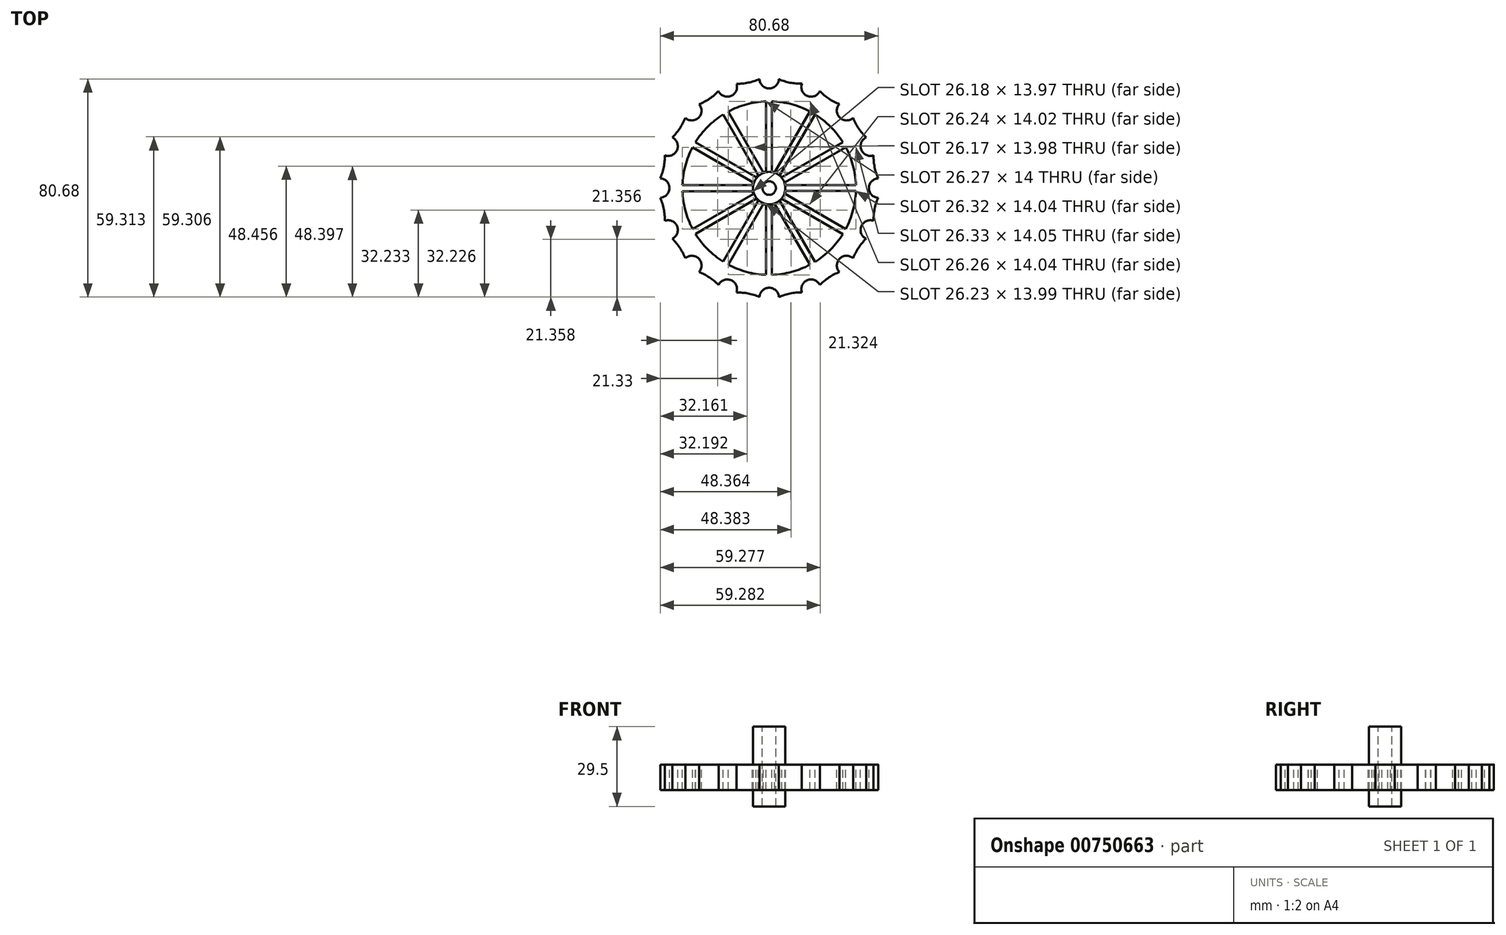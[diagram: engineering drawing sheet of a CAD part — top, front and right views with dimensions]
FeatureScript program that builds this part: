
annotation { "Feature Type Name" : "Feature", "Feature Type Description" : "" }
export const myFeature = defineFeature(function(context is Context, id is Id, definition is map)
    precondition{}
    {
        {
            var Q0;
            Q0=qCreatedBy(makeId("Front.planeOp"),FACE);
            var sketch = newSketch(context, id + "F0", { "sketchPlane" : qUnion([Q0])});
            skLineSegment(sketch, "E0", {"start": v(2.5, 29.5) * mm, "end": v(2.5, 0) * mm});
            skLineSegment(sketch, "E1", {"start": v(2.5, 0) * mm, "end": v(6, 0) * mm});
            skLineSegment(sketch, "E2", {"start": v(6, 0) * mm, "end": v(6, 6) * mm});
            skLineSegment(sketch, "E3", {"start": v(6, 6) * mm, "end": v(40.5, 6) * mm});
            skLineSegment(sketch, "E4", {"start": v(40.5, 6) * mm, "end": v(40.5, 15.5) * mm});
            skLineSegment(sketch, "E5", {"start": v(40.5, 15.5) * mm, "end": v(6, 15.5) * mm});
            skLineSegment(sketch, "E6", {"start": v(6, 15.5) * mm, "end": v(6, 29.5) * mm});
            skLineSegment(sketch, "E7", {"start": v(6, 29.5) * mm, "end": v(2.5, 29.5) * mm});
            skLineSegment(sketch, "E8", {"start": v(0, 75.26) * mm, "end": v(0, -74.89) * mm});
            skSolve(sketch);
        }
        {
            var Q0;
            Q0=makeQuery(id+"F0.imprint","IMPRINT",FACE,{"disambiguationData":[TD([[makeQuery(id+"F0.imprint","IMPRINT",EDGE,{"derivedFrom":sQuery(id+"F0.wireOp",EDGE,"E0")}),1.0]])]});
            var Q1;
            Q1=sQuery(id+"F0.wireOp",EDGE,"E8");
            revolve(context, id + "F1", {"surfaceOperationType" : NewSurfaceOperationType.NEW, "entities" : qUnion([Q0]), "axis" : qUnion([Q1]), "revolveType" : RevolveType.FULL});
        }
        {
            var Q0;
            Q0=makeQuery(id+"F1.opRevolve","SWEPT_FACE",FACE,{"disambiguationData":[OSD([sQuery(id+"F0.wireOp",EDGE,"E5")])]});
            var sketch = newSketch(context, id + "F2", { "sketchPlane" : qUnion([Q0])});
            skCircle(sketch, "E9", {"center": v(40.5, 0) * mm, "radius": 3.6 * mm});
            skCircle(sketch, "E10.1.0", {"center": v(37.42, 15.5) * mm, "radius": 3.6 * mm});
            skCircle(sketch, "E10.2.0", {"center": v(28.64, 28.64) * mm, "radius": 3.6 * mm});
            skCircle(sketch, "E10.3.0", {"center": v(15.5, 37.42) * mm, "radius": 3.6 * mm});
            skCircle(sketch, "E10.4.0", {"center": v(0, 40.5) * mm, "radius": 3.6 * mm});
            skCircle(sketch, "E10.5.0", {"center": v(-15.5, 37.42) * mm, "radius": 3.6 * mm});
            skCircle(sketch, "E10.6.0", {"center": v(-28.64, 28.64) * mm, "radius": 3.6 * mm});
            skCircle(sketch, "E10.7.0", {"center": v(-37.42, 15.5) * mm, "radius": 3.6 * mm});
            skCircle(sketch, "E10.8.0", {"center": v(-40.5, 0) * mm, "radius": 3.6 * mm});
            skCircle(sketch, "E10.9.0", {"center": v(-37.42, -15.5) * mm, "radius": 3.6 * mm});
            skCircle(sketch, "E10.10.0", {"center": v(-28.64, -28.64) * mm, "radius": 3.6 * mm});
            skCircle(sketch, "E10.11.0", {"center": v(-15.5, -37.42) * mm, "radius": 3.6 * mm});
            skCircle(sketch, "E10.12.0", {"center": v(0, -40.5) * mm, "radius": 3.6 * mm});
            skCircle(sketch, "E10.13.0", {"center": v(15.5, -37.42) * mm, "radius": 3.6 * mm});
            skCircle(sketch, "E10.14.0", {"center": v(28.64, -28.64) * mm, "radius": 3.6 * mm});
            skCircle(sketch, "E10.15.0", {"center": v(37.42, -15.5) * mm, "radius": 3.6 * mm});
            skPoint(sketch, "E10.center", {"position": v(0, 0) * mm});
            skArc(sketch, "E11", {"start": v(38.6, 12.1) * mm, "mid": v(39.02, 7.76) * mm, "end": v(40.34, 3.6) * mm});
            skArc(sketch, "E12.1.0", {"start": v(31.04, 25.96) * mm, "mid": v(33.08, 22.1) * mm, "end": v(35.9, 18.76) * mm});
            skArc(sketch, "E12.2.0", {"start": v(18.74, 35.86) * mm, "mid": v(22.1, 33.07) * mm, "end": v(25.98, 31.07) * mm});
            skArc(sketch, "E12.3.0", {"start": v(3.6, 40.3) * mm, "mid": v(7.77, 39.01) * mm, "end": v(12.11, 38.65) * mm});
            skArc(sketch, "E12.4.0", {"start": v(-12.1, 38.6) * mm, "mid": v(-7.76, 39.02) * mm, "end": v(-3.6, 40.34) * mm});
            skArc(sketch, "E12.5.0", {"start": v(-25.96, 31.04) * mm, "mid": v(-22.1, 33.08) * mm, "end": v(-18.76, 35.9) * mm});
            skArc(sketch, "E12.6.0", {"start": v(-35.86, 18.74) * mm, "mid": v(-33.07, 22.1) * mm, "end": v(-31.07, 25.98) * mm});
            skArc(sketch, "E12.7.0", {"start": v(-40.3, 3.6) * mm, "mid": v(-39.01, 7.77) * mm, "end": v(-38.65, 12.11) * mm});
            skArc(sketch, "E12.8.0", {"start": v(-38.6, -12.1) * mm, "mid": v(-39.02, -7.76) * mm, "end": v(-40.34, -3.6) * mm});
            skArc(sketch, "E12.9.0", {"start": v(-31.04, -25.96) * mm, "mid": v(-33.08, -22.1) * mm, "end": v(-35.9, -18.76) * mm});
            skArc(sketch, "E12.10.0", {"start": v(-18.74, -35.86) * mm, "mid": v(-22.1, -33.07) * mm, "end": v(-25.98, -31.07) * mm});
            skArc(sketch, "E12.11.0", {"start": v(-3.6, -40.3) * mm, "mid": v(-7.77, -39.01) * mm, "end": v(-12.11, -38.65) * mm});
            skArc(sketch, "E12.12.0", {"start": v(12.1, -38.6) * mm, "mid": v(7.76, -39.02) * mm, "end": v(3.6, -40.34) * mm});
            skArc(sketch, "E12.13.0", {"start": v(25.96, -31.04) * mm, "mid": v(22.1, -33.08) * mm, "end": v(18.76, -35.9) * mm});
            skArc(sketch, "E12.14.0", {"start": v(35.86, -18.74) * mm, "mid": v(33.07, -22.1) * mm, "end": v(31.07, -25.98) * mm});
            skArc(sketch, "E12.15.0", {"start": v(40.3, -3.6) * mm, "mid": v(39.01, -7.77) * mm, "end": v(38.65, -12.11) * mm});
            skSolve(sketch);
        }
        {
            var Q0;
            {var subQ0=sQuery(id+"F2.wireOp",EDGE,"E9");var subQ1=makeQuery(id+"F1.opRevolve","SWEPT_EDGE",EDGE,{"disambiguationData":[OSD([sQuery(id+"F0.wireOp",EDGE,"E4"),sQuery(id+"F0.wireOp",EDGE,"E5")])]});var subQ3=makeQuery(id+"F2.imprint","INTERSECT",VERTEX,{"derivedFrom":[subQ1,subQ0]});Q0=makeQuery(id+"F2.imprint","IMPRINT",FACE,{"disambiguationData":[TD([[makeQuery(id+"F2.imprint","IMPRINT",EDGE,{"disambiguationData":[TD([[subQ3,-1.0]])],"derivedFrom":subQ0}),1.0]])]});}
            var Q1;
            {var subQ0=sQuery(id+"F2.wireOp",EDGE,"E10.1.0");var subQ1=makeQuery(id+"F1.opRevolve","SWEPT_EDGE",EDGE,{"disambiguationData":[OSD([sQuery(id+"F0.wireOp",EDGE,"E4"),sQuery(id+"F0.wireOp",EDGE,"E5")])]});var subQ3=makeQuery(id+"F2.imprint","INTERSECT",VERTEX,{"derivedFrom":[subQ1,subQ0]});Q1=makeQuery(id+"F2.imprint","IMPRINT",FACE,{"disambiguationData":[TD([[makeQuery(id+"F2.imprint","IMPRINT",EDGE,{"disambiguationData":[TD([[subQ3,-1.0]])],"derivedFrom":subQ0}),1.0]])]});}
            var Q2;
            {var subQ0=sQuery(id+"F2.wireOp",EDGE,"E10.2.0");var subQ1=makeQuery(id+"F1.opRevolve","SWEPT_EDGE",EDGE,{"disambiguationData":[OSD([sQuery(id+"F0.wireOp",EDGE,"E4"),sQuery(id+"F0.wireOp",EDGE,"E5")])]});var subQ3=makeQuery(id+"F2.imprint","INTERSECT",VERTEX,{"derivedFrom":[subQ1,subQ0]});Q2=makeQuery(id+"F2.imprint","IMPRINT",FACE,{"disambiguationData":[TD([[makeQuery(id+"F2.imprint","IMPRINT",EDGE,{"disambiguationData":[TD([[subQ3,-1.0]])],"derivedFrom":subQ0}),1.0]])]});}
            var Q3;
            {var subQ0=sQuery(id+"F2.wireOp",EDGE,"E10.3.0");var subQ1=makeQuery(id+"F1.opRevolve","SWEPT_EDGE",EDGE,{"disambiguationData":[OSD([sQuery(id+"F0.wireOp",EDGE,"E4"),sQuery(id+"F0.wireOp",EDGE,"E5")])]});var subQ3=makeQuery(id+"F2.imprint","INTERSECT",VERTEX,{"derivedFrom":[subQ1,subQ0]});Q3=makeQuery(id+"F2.imprint","IMPRINT",FACE,{"disambiguationData":[TD([[makeQuery(id+"F2.imprint","IMPRINT",EDGE,{"disambiguationData":[TD([[subQ3,-1.0]])],"derivedFrom":subQ0}),1.0]])]});}
            var Q4;
            {var subQ0=sQuery(id+"F2.wireOp",EDGE,"E10.4.0");var subQ1=makeQuery(id+"F1.opRevolve","SWEPT_EDGE",EDGE,{"disambiguationData":[OSD([sQuery(id+"F0.wireOp",EDGE,"E4"),sQuery(id+"F0.wireOp",EDGE,"E5")])]});var subQ3=makeQuery(id+"F2.imprint","INTERSECT",VERTEX,{"derivedFrom":[subQ1,subQ0]});Q4=makeQuery(id+"F2.imprint","IMPRINT",FACE,{"disambiguationData":[TD([[makeQuery(id+"F2.imprint","IMPRINT",EDGE,{"disambiguationData":[TD([[subQ3,-1.0]])],"derivedFrom":subQ0}),1.0]])]});}
            var Q5;
            {var subQ0=sQuery(id+"F2.wireOp",EDGE,"E10.5.0");var subQ1=makeQuery(id+"F1.opRevolve","SWEPT_EDGE",EDGE,{"disambiguationData":[OSD([sQuery(id+"F0.wireOp",EDGE,"E4"),sQuery(id+"F0.wireOp",EDGE,"E5")])]});var subQ3=makeQuery(id+"F2.imprint","INTERSECT",VERTEX,{"derivedFrom":[subQ1,subQ0]});Q5=makeQuery(id+"F2.imprint","IMPRINT",FACE,{"disambiguationData":[TD([[makeQuery(id+"F2.imprint","IMPRINT",EDGE,{"disambiguationData":[TD([[subQ3,-1.0]])],"derivedFrom":subQ0}),1.0]])]});}
            var Q6;
            {var subQ0=sQuery(id+"F2.wireOp",EDGE,"E10.6.0");var subQ1=makeQuery(id+"F1.opRevolve","SWEPT_EDGE",EDGE,{"disambiguationData":[OSD([sQuery(id+"F0.wireOp",EDGE,"E4"),sQuery(id+"F0.wireOp",EDGE,"E5")])]});var subQ3=makeQuery(id+"F2.imprint","INTERSECT",VERTEX,{"derivedFrom":[subQ1,subQ0]});Q6=makeQuery(id+"F2.imprint","IMPRINT",FACE,{"disambiguationData":[TD([[makeQuery(id+"F2.imprint","IMPRINT",EDGE,{"disambiguationData":[TD([[subQ3,-1.0]])],"derivedFrom":subQ0}),1.0]])]});}
            var Q7;
            {var subQ0=sQuery(id+"F2.wireOp",EDGE,"E10.7.0");var subQ1=makeQuery(id+"F1.opRevolve","SWEPT_EDGE",EDGE,{"disambiguationData":[OSD([sQuery(id+"F0.wireOp",EDGE,"E4"),sQuery(id+"F0.wireOp",EDGE,"E5")])]});var subQ3=makeQuery(id+"F2.imprint","INTERSECT",VERTEX,{"derivedFrom":[subQ1,subQ0]});Q7=makeQuery(id+"F2.imprint","IMPRINT",FACE,{"disambiguationData":[TD([[makeQuery(id+"F2.imprint","IMPRINT",EDGE,{"disambiguationData":[TD([[subQ3,-1.0]])],"derivedFrom":subQ0}),1.0]])]});}
            var Q8;
            {var subQ0=sQuery(id+"F2.wireOp",EDGE,"E10.8.0");var subQ1=makeQuery(id+"F1.opRevolve","SWEPT_EDGE",EDGE,{"disambiguationData":[OSD([sQuery(id+"F0.wireOp",EDGE,"E4"),sQuery(id+"F0.wireOp",EDGE,"E5")])]});var subQ3=makeQuery(id+"F2.imprint","INTERSECT",VERTEX,{"derivedFrom":[subQ1,subQ0]});Q8=makeQuery(id+"F2.imprint","IMPRINT",FACE,{"disambiguationData":[TD([[makeQuery(id+"F2.imprint","IMPRINT",EDGE,{"disambiguationData":[TD([[subQ3,-1.0]])],"derivedFrom":subQ0}),1.0]])]});}
            var Q9;
            {var subQ0=sQuery(id+"F2.wireOp",EDGE,"E10.9.0");var subQ1=makeQuery(id+"F1.opRevolve","SWEPT_EDGE",EDGE,{"disambiguationData":[OSD([sQuery(id+"F0.wireOp",EDGE,"E4"),sQuery(id+"F0.wireOp",EDGE,"E5")])]});var subQ3=makeQuery(id+"F2.imprint","INTERSECT",VERTEX,{"derivedFrom":[subQ1,subQ0]});Q9=makeQuery(id+"F2.imprint","IMPRINT",FACE,{"disambiguationData":[TD([[makeQuery(id+"F2.imprint","IMPRINT",EDGE,{"disambiguationData":[TD([[subQ3,-1.0]])],"derivedFrom":subQ0}),1.0]])]});}
            var Q10;
            {var subQ0=sQuery(id+"F2.wireOp",EDGE,"E10.10.0");var subQ1=makeQuery(id+"F1.opRevolve","SWEPT_EDGE",EDGE,{"disambiguationData":[OSD([sQuery(id+"F0.wireOp",EDGE,"E4"),sQuery(id+"F0.wireOp",EDGE,"E5")])]});var subQ3=makeQuery(id+"F2.imprint","INTERSECT",VERTEX,{"derivedFrom":[subQ1,subQ0]});Q10=makeQuery(id+"F2.imprint","IMPRINT",FACE,{"disambiguationData":[TD([[makeQuery(id+"F2.imprint","IMPRINT",EDGE,{"disambiguationData":[TD([[subQ3,-1.0]])],"derivedFrom":subQ0}),1.0]])]});}
            var Q11;
            {var subQ0=sQuery(id+"F2.wireOp",EDGE,"E10.11.0");var subQ1=makeQuery(id+"F1.opRevolve","SWEPT_EDGE",EDGE,{"disambiguationData":[OSD([sQuery(id+"F0.wireOp",EDGE,"E4"),sQuery(id+"F0.wireOp",EDGE,"E5")])]});var subQ3=makeQuery(id+"F2.imprint","INTERSECT",VERTEX,{"derivedFrom":[subQ1,subQ0]});Q11=makeQuery(id+"F2.imprint","IMPRINT",FACE,{"disambiguationData":[TD([[makeQuery(id+"F2.imprint","IMPRINT",EDGE,{"disambiguationData":[TD([[subQ3,-1.0]])],"derivedFrom":subQ0}),1.0]])]});}
            var Q12;
            {var subQ0=sQuery(id+"F2.wireOp",EDGE,"E10.12.0");var subQ1=makeQuery(id+"F1.opRevolve","SWEPT_EDGE",EDGE,{"disambiguationData":[OSD([sQuery(id+"F0.wireOp",EDGE,"E4"),sQuery(id+"F0.wireOp",EDGE,"E5")])]});var subQ3=makeQuery(id+"F2.imprint","INTERSECT",VERTEX,{"derivedFrom":[subQ1,subQ0]});Q12=makeQuery(id+"F2.imprint","IMPRINT",FACE,{"disambiguationData":[TD([[makeQuery(id+"F2.imprint","IMPRINT",EDGE,{"disambiguationData":[TD([[subQ3,-1.0]])],"derivedFrom":subQ0}),1.0]])]});}
            var Q13;
            {var subQ0=sQuery(id+"F2.wireOp",EDGE,"E10.13.0");var subQ1=makeQuery(id+"F1.opRevolve","SWEPT_EDGE",EDGE,{"disambiguationData":[OSD([sQuery(id+"F0.wireOp",EDGE,"E4"),sQuery(id+"F0.wireOp",EDGE,"E5")])]});var subQ3=makeQuery(id+"F2.imprint","INTERSECT",VERTEX,{"derivedFrom":[subQ1,subQ0]});Q13=makeQuery(id+"F2.imprint","IMPRINT",FACE,{"disambiguationData":[TD([[makeQuery(id+"F2.imprint","IMPRINT",EDGE,{"disambiguationData":[TD([[subQ3,-1.0]])],"derivedFrom":subQ0}),1.0]])]});}
            var Q14;
            {var subQ0=sQuery(id+"F2.wireOp",EDGE,"E10.14.0");var subQ1=makeQuery(id+"F1.opRevolve","SWEPT_EDGE",EDGE,{"disambiguationData":[OSD([sQuery(id+"F0.wireOp",EDGE,"E4"),sQuery(id+"F0.wireOp",EDGE,"E5")])]});var subQ3=makeQuery(id+"F2.imprint","INTERSECT",VERTEX,{"derivedFrom":[subQ1,subQ0]});Q14=makeQuery(id+"F2.imprint","IMPRINT",FACE,{"disambiguationData":[TD([[makeQuery(id+"F2.imprint","IMPRINT",EDGE,{"disambiguationData":[TD([[subQ3,-1.0]])],"derivedFrom":subQ0}),1.0]])]});}
            var Q15;
            {var subQ0=sQuery(id+"F2.wireOp",EDGE,"E10.15.0");var subQ1=makeQuery(id+"F1.opRevolve","SWEPT_EDGE",EDGE,{"disambiguationData":[OSD([sQuery(id+"F0.wireOp",EDGE,"E4"),sQuery(id+"F0.wireOp",EDGE,"E5")])]});var subQ3=makeQuery(id+"F2.imprint","INTERSECT",VERTEX,{"derivedFrom":[subQ1,subQ0]});Q15=makeQuery(id+"F2.imprint","IMPRINT",FACE,{"disambiguationData":[TD([[makeQuery(id+"F2.imprint","IMPRINT",EDGE,{"disambiguationData":[TD([[subQ3,-1.0]])],"derivedFrom":subQ0}),1.0]])]});}
            var Q16;
            {var subQ0=sQuery(id+"F2.wireOp",EDGE,"E9");var subQ3=makeQuery(id+"F2.imprint","INTERSECT",VERTEX,{"derivedFrom":[subQ0,sQuery(id+"F2.wireOp",EDGE,"E12.15.0")]});Q16=makeQuery(id+"F2.imprint","IMPRINT",FACE,{"disambiguationData":[TD([[makeQuery(id+"F2.imprint","IMPRINT",EDGE,{"disambiguationData":[TD([[subQ3,-1.0]])],"derivedFrom":subQ0}),1.0]])]});}
            var Q17;
            {var subQ0=sQuery(id+"F2.wireOp",EDGE,"E10.1.0");var subQ1=makeQuery(id+"F2.imprint","INTERSECT",VERTEX,{"derivedFrom":[subQ0,sQuery(id+"F2.wireOp",EDGE,"E11")]});Q17=makeQuery(id+"F2.imprint","IMPRINT",FACE,{"disambiguationData":[TD([[makeQuery(id+"F2.imprint","IMPRINT",EDGE,{"disambiguationData":[TD([[subQ1,-1.0]])],"derivedFrom":subQ0}),1.0]])]});}
            var Q18;
            {var subQ0=sQuery(id+"F2.wireOp",EDGE,"E10.2.0");var subQ1=makeQuery(id+"F2.imprint","INTERSECT",VERTEX,{"derivedFrom":[subQ0,sQuery(id+"F2.wireOp",EDGE,"E12.1.0")]});Q18=makeQuery(id+"F2.imprint","IMPRINT",FACE,{"disambiguationData":[TD([[makeQuery(id+"F2.imprint","IMPRINT",EDGE,{"disambiguationData":[TD([[subQ1,-1.0]])],"derivedFrom":subQ0}),1.0]])]});}
            var Q19;
            {var subQ0=sQuery(id+"F2.wireOp",EDGE,"E10.3.0");var subQ1=makeQuery(id+"F2.imprint","INTERSECT",VERTEX,{"derivedFrom":[subQ0,sQuery(id+"F2.wireOp",EDGE,"E12.2.0")]});Q19=makeQuery(id+"F2.imprint","IMPRINT",FACE,{"disambiguationData":[TD([[makeQuery(id+"F2.imprint","IMPRINT",EDGE,{"disambiguationData":[TD([[subQ1,-1.0]])],"derivedFrom":subQ0}),1.0]])]});}
            var Q20;
            {var subQ0=sQuery(id+"F2.wireOp",EDGE,"E10.4.0");var subQ1=makeQuery(id+"F2.imprint","INTERSECT",VERTEX,{"derivedFrom":[subQ0,sQuery(id+"F2.wireOp",EDGE,"E12.3.0")]});Q20=makeQuery(id+"F2.imprint","IMPRINT",FACE,{"disambiguationData":[TD([[makeQuery(id+"F2.imprint","IMPRINT",EDGE,{"disambiguationData":[TD([[subQ1,-1.0]])],"derivedFrom":subQ0}),1.0]])]});}
            var Q21;
            {var subQ0=sQuery(id+"F2.wireOp",EDGE,"E10.5.0");var subQ1=makeQuery(id+"F2.imprint","INTERSECT",VERTEX,{"derivedFrom":[subQ0,sQuery(id+"F2.wireOp",EDGE,"E12.4.0")]});Q21=makeQuery(id+"F2.imprint","IMPRINT",FACE,{"disambiguationData":[TD([[makeQuery(id+"F2.imprint","IMPRINT",EDGE,{"disambiguationData":[TD([[subQ1,-1.0]])],"derivedFrom":subQ0}),1.0]])]});}
            var Q22;
            {var subQ0=sQuery(id+"F2.wireOp",EDGE,"E10.6.0");var subQ1=makeQuery(id+"F2.imprint","INTERSECT",VERTEX,{"derivedFrom":[subQ0,sQuery(id+"F2.wireOp",EDGE,"E12.5.0")]});Q22=makeQuery(id+"F2.imprint","IMPRINT",FACE,{"disambiguationData":[TD([[makeQuery(id+"F2.imprint","IMPRINT",EDGE,{"disambiguationData":[TD([[subQ1,-1.0]])],"derivedFrom":subQ0}),1.0]])]});}
            var Q23;
            {var subQ0=sQuery(id+"F2.wireOp",EDGE,"E10.7.0");var subQ1=makeQuery(id+"F2.imprint","INTERSECT",VERTEX,{"derivedFrom":[subQ0,sQuery(id+"F2.wireOp",EDGE,"E12.6.0")]});Q23=makeQuery(id+"F2.imprint","IMPRINT",FACE,{"disambiguationData":[TD([[makeQuery(id+"F2.imprint","IMPRINT",EDGE,{"disambiguationData":[TD([[subQ1,-1.0]])],"derivedFrom":subQ0}),1.0]])]});}
            var Q24;
            {var subQ0=sQuery(id+"F2.wireOp",EDGE,"E10.8.0");var subQ1=makeQuery(id+"F2.imprint","INTERSECT",VERTEX,{"derivedFrom":[subQ0,sQuery(id+"F2.wireOp",EDGE,"E12.7.0")]});Q24=makeQuery(id+"F2.imprint","IMPRINT",FACE,{"disambiguationData":[TD([[makeQuery(id+"F2.imprint","IMPRINT",EDGE,{"disambiguationData":[TD([[subQ1,-1.0]])],"derivedFrom":subQ0}),1.0]])]});}
            var Q25;
            {var subQ0=sQuery(id+"F2.wireOp",EDGE,"E10.9.0");var subQ1=makeQuery(id+"F2.imprint","INTERSECT",VERTEX,{"derivedFrom":[subQ0,sQuery(id+"F2.wireOp",EDGE,"E12.8.0")]});Q25=makeQuery(id+"F2.imprint","IMPRINT",FACE,{"disambiguationData":[TD([[makeQuery(id+"F2.imprint","IMPRINT",EDGE,{"disambiguationData":[TD([[subQ1,-1.0]])],"derivedFrom":subQ0}),1.0]])]});}
            var Q26;
            {var subQ0=sQuery(id+"F2.wireOp",EDGE,"E10.10.0");var subQ1=makeQuery(id+"F2.imprint","INTERSECT",VERTEX,{"derivedFrom":[subQ0,sQuery(id+"F2.wireOp",EDGE,"E12.9.0")]});Q26=makeQuery(id+"F2.imprint","IMPRINT",FACE,{"disambiguationData":[TD([[makeQuery(id+"F2.imprint","IMPRINT",EDGE,{"disambiguationData":[TD([[subQ1,-1.0]])],"derivedFrom":subQ0}),1.0]])]});}
            var Q27;
            {var subQ0=sQuery(id+"F2.wireOp",EDGE,"E10.11.0");var subQ1=makeQuery(id+"F2.imprint","INTERSECT",VERTEX,{"derivedFrom":[subQ0,sQuery(id+"F2.wireOp",EDGE,"E12.10.0")]});Q27=makeQuery(id+"F2.imprint","IMPRINT",FACE,{"disambiguationData":[TD([[makeQuery(id+"F2.imprint","IMPRINT",EDGE,{"disambiguationData":[TD([[subQ1,-1.0]])],"derivedFrom":subQ0}),1.0]])]});}
            var Q28;
            {var subQ0=sQuery(id+"F2.wireOp",EDGE,"E10.12.0");var subQ1=makeQuery(id+"F2.imprint","INTERSECT",VERTEX,{"derivedFrom":[subQ0,sQuery(id+"F2.wireOp",EDGE,"E12.11.0")]});Q28=makeQuery(id+"F2.imprint","IMPRINT",FACE,{"disambiguationData":[TD([[makeQuery(id+"F2.imprint","IMPRINT",EDGE,{"disambiguationData":[TD([[subQ1,-1.0]])],"derivedFrom":subQ0}),1.0]])]});}
            var Q29;
            {var subQ0=sQuery(id+"F2.wireOp",EDGE,"E10.13.0");var subQ1=makeQuery(id+"F2.imprint","INTERSECT",VERTEX,{"derivedFrom":[subQ0,sQuery(id+"F2.wireOp",EDGE,"E12.12.0")]});Q29=makeQuery(id+"F2.imprint","IMPRINT",FACE,{"disambiguationData":[TD([[makeQuery(id+"F2.imprint","IMPRINT",EDGE,{"disambiguationData":[TD([[subQ1,-1.0]])],"derivedFrom":subQ0}),1.0]])]});}
            var Q30;
            {var subQ0=sQuery(id+"F2.wireOp",EDGE,"E10.14.0");var subQ1=makeQuery(id+"F2.imprint","INTERSECT",VERTEX,{"derivedFrom":[subQ0,sQuery(id+"F2.wireOp",EDGE,"E12.13.0")]});Q30=makeQuery(id+"F2.imprint","IMPRINT",FACE,{"disambiguationData":[TD([[makeQuery(id+"F2.imprint","IMPRINT",EDGE,{"disambiguationData":[TD([[subQ1,-1.0]])],"derivedFrom":subQ0}),1.0]])]});}
            var Q31;
            {var subQ0=sQuery(id+"F2.wireOp",EDGE,"E10.15.0");var subQ1=makeQuery(id+"F2.imprint","INTERSECT",VERTEX,{"derivedFrom":[subQ0,sQuery(id+"F2.wireOp",EDGE,"E12.14.0")]});Q31=makeQuery(id+"F2.imprint","IMPRINT",FACE,{"disambiguationData":[TD([[makeQuery(id+"F2.imprint","IMPRINT",EDGE,{"disambiguationData":[TD([[subQ1,-1.0]])],"derivedFrom":subQ0}),1.0]])]});}
            var Q32;
            {var subQ0=sQuery(id+"F2.wireOp",EDGE,"E11");Q32=makeQuery(id+"F2.imprint","IMPRINT",FACE,{"disambiguationData":[TD([[makeQuery(id+"F2.imprint","IMPRINT",EDGE,{"derivedFrom":subQ0}),1.0]])]});}
            var Q33;
            {var subQ0=sQuery(id+"F2.wireOp",EDGE,"E12.1.0");Q33=makeQuery(id+"F2.imprint","IMPRINT",FACE,{"disambiguationData":[TD([[makeQuery(id+"F2.imprint","IMPRINT",EDGE,{"derivedFrom":subQ0}),1.0]])]});}
            var Q34;
            {var subQ0=sQuery(id+"F2.wireOp",EDGE,"E12.13.0");Q34=makeQuery(id+"F2.imprint","IMPRINT",FACE,{"disambiguationData":[TD([[makeQuery(id+"F2.imprint","IMPRINT",EDGE,{"derivedFrom":subQ0}),1.0]])]});}
            var Q35;
            {var subQ0=sQuery(id+"F2.wireOp",EDGE,"E12.2.0");Q35=makeQuery(id+"F2.imprint","IMPRINT",FACE,{"disambiguationData":[TD([[makeQuery(id+"F2.imprint","IMPRINT",EDGE,{"derivedFrom":subQ0}),1.0]])]});}
            var Q36;
            {var subQ0=sQuery(id+"F2.wireOp",EDGE,"E12.14.0");Q36=makeQuery(id+"F2.imprint","IMPRINT",FACE,{"disambiguationData":[TD([[makeQuery(id+"F2.imprint","IMPRINT",EDGE,{"derivedFrom":subQ0}),1.0]])]});}
            var Q37;
            {var subQ0=sQuery(id+"F2.wireOp",EDGE,"E12.15.0");Q37=makeQuery(id+"F2.imprint","IMPRINT",FACE,{"disambiguationData":[TD([[makeQuery(id+"F2.imprint","IMPRINT",EDGE,{"derivedFrom":subQ0}),1.0]])]});}
            var Q38;
            {var subQ0=sQuery(id+"F2.wireOp",EDGE,"E12.7.0");Q38=makeQuery(id+"F2.imprint","IMPRINT",FACE,{"disambiguationData":[TD([[makeQuery(id+"F2.imprint","IMPRINT",EDGE,{"derivedFrom":subQ0}),1.0]])]});}
            var Q39;
            {var subQ0=sQuery(id+"F2.wireOp",EDGE,"E12.8.0");Q39=makeQuery(id+"F2.imprint","IMPRINT",FACE,{"disambiguationData":[TD([[makeQuery(id+"F2.imprint","IMPRINT",EDGE,{"derivedFrom":subQ0}),1.0]])]});}
            var Q40;
            {var subQ0=sQuery(id+"F2.wireOp",EDGE,"E12.9.0");Q40=makeQuery(id+"F2.imprint","IMPRINT",FACE,{"disambiguationData":[TD([[makeQuery(id+"F2.imprint","IMPRINT",EDGE,{"derivedFrom":subQ0}),1.0]])]});}
            var Q41;
            {var subQ0=sQuery(id+"F2.wireOp",EDGE,"E12.6.0");Q41=makeQuery(id+"F2.imprint","IMPRINT",FACE,{"disambiguationData":[TD([[makeQuery(id+"F2.imprint","IMPRINT",EDGE,{"derivedFrom":subQ0}),1.0]])]});}
            var Q42;
            {var subQ0=sQuery(id+"F2.wireOp",EDGE,"E12.10.0");Q42=makeQuery(id+"F2.imprint","IMPRINT",FACE,{"disambiguationData":[TD([[makeQuery(id+"F2.imprint","IMPRINT",EDGE,{"derivedFrom":subQ0}),1.0]])]});}
            var Q43;
            {var subQ0=sQuery(id+"F2.wireOp",EDGE,"E12.5.0");Q43=makeQuery(id+"F2.imprint","IMPRINT",FACE,{"disambiguationData":[TD([[makeQuery(id+"F2.imprint","IMPRINT",EDGE,{"derivedFrom":subQ0}),1.0]])]});}
            var Q44;
            {var subQ0=sQuery(id+"F2.wireOp",EDGE,"E12.4.0");Q44=makeQuery(id+"F2.imprint","IMPRINT",FACE,{"disambiguationData":[TD([[makeQuery(id+"F2.imprint","IMPRINT",EDGE,{"derivedFrom":subQ0}),1.0]])]});}
            var Q45;
            {var subQ0=sQuery(id+"F2.wireOp",EDGE,"E12.11.0");Q45=makeQuery(id+"F2.imprint","IMPRINT",FACE,{"disambiguationData":[TD([[makeQuery(id+"F2.imprint","IMPRINT",EDGE,{"derivedFrom":subQ0}),1.0]])]});}
            var Q46;
            {var subQ0=sQuery(id+"F2.wireOp",EDGE,"E12.12.0");Q46=makeQuery(id+"F2.imprint","IMPRINT",FACE,{"disambiguationData":[TD([[makeQuery(id+"F2.imprint","IMPRINT",EDGE,{"derivedFrom":subQ0}),1.0]])]});}
            var Q47;
            {var subQ0=sQuery(id+"F2.wireOp",EDGE,"E12.3.0");Q47=makeQuery(id+"F2.imprint","IMPRINT",FACE,{"disambiguationData":[TD([[makeQuery(id+"F2.imprint","IMPRINT",EDGE,{"derivedFrom":subQ0}),1.0]])]});}
            extrude(context, id + "F3", {"entities" : qUnion([Q0, Q1, Q2, Q3, Q4, Q5, Q6, Q7, Q8, Q9, Q10, Q11, Q12, Q13, Q14, Q15, Q16, Q17, Q18, Q19, Q20, Q21, Q22, Q23, Q24, Q25, Q26, Q27, Q28, Q29, Q30, Q31, Q32, Q33, Q34, Q35, Q36, Q37, Q38, Q39, Q40, Q41, Q42, Q43, Q44, Q45, Q46, Q47]), "operationType" : NewBodyOperationType.REMOVE, "endBound" : BoundingType.THROUGH_ALL, "oppositeDirection" : true, "depth" : 25 * mm, "offsetDistance" : 25 * mm});
        }
        {
            var Q0;
            Q0=makeQuery(id+"F1.opRevolve","SWEPT_FACE",FACE,{"disambiguationData":[OSD([sQuery(id+"F0.wireOp",EDGE,"E5")])]});
            var sketch = newSketch(context, id + "F4", { "sketchPlane" : qUnion([Q0])});
            skCircle(sketch, "E13", {"center": v(0, 0) * mm, "radius": 32.12 * mm});
            skLineSegment(sketch, "E14", {"start": v(0, 0) * mm, "end": v(32.12, 0) * mm});
            skLineSegment(sketch, "E15", {"start": v(5.9, 1.1) * mm, "end": v(32.1, 1.1) * mm});
            skLineSegment(sketch, "E16.MirrorCS", {"start": v(5.9, -1.1) * mm, "end": v(32.1, -1.1) * mm});
            skLineSegment(sketch, "E17.1.0", {"start": v(4.55, 3.93) * mm, "end": v(27.24, 17.03) * mm});
            skLineSegment(sketch, "E17.1.1", {"start": v(5.64, 2.04) * mm, "end": v(28.33, 15.14) * mm});
            skLineSegment(sketch, "E17.2.0", {"start": v(1.96, 5.71) * mm, "end": v(15.06, 28.4) * mm});
            skLineSegment(sketch, "E17.2.1", {"start": v(3.85, 4.62) * mm, "end": v(16.95, 27.31) * mm});
            skLineSegment(sketch, "E17.3.0", {"start": v(-1.18, 5.96) * mm, "end": v(-1.18, 32.16) * mm});
            skLineSegment(sketch, "E17.3.1", {"start": v(1, 5.96) * mm, "end": v(1, 32.16) * mm});
            skLineSegment(sketch, "E17.4.0", {"start": v(-4.02, 4.6) * mm, "end": v(-17.12, 27.3) * mm});
            skLineSegment(sketch, "E17.4.1", {"start": v(-2.13, 5.7) * mm, "end": v(-15.23, 28.4) * mm});
            skLineSegment(sketch, "E17.5.0", {"start": v(-5.8, 2.02) * mm, "end": v(-28.5, 15.12) * mm});
            skLineSegment(sketch, "E17.5.1", {"start": v(-4.7, 3.9) * mm, "end": v(-27.4, 17) * mm});
            skLineSegment(sketch, "E17.6.0", {"start": v(-6.05, -1.12) * mm, "end": v(-32.25, -1.12) * mm});
            skLineSegment(sketch, "E17.6.1", {"start": v(-6.05, 1.07) * mm, "end": v(-32.25, 1.07) * mm});
            skLineSegment(sketch, "E17.7.0", {"start": v(-4.7, -3.96) * mm, "end": v(-27.39, -17.06) * mm});
            skLineSegment(sketch, "E17.7.1", {"start": v(-5.79, -2.07) * mm, "end": v(-28.48, -15.17) * mm});
            skLineSegment(sketch, "E17.8.0", {"start": v(-2.1, -5.74) * mm, "end": v(-15.2, -28.43) * mm});
            skLineSegment(sketch, "E17.8.1", {"start": v(-4, -4.65) * mm, "end": v(-17.1, -27.34) * mm});
            skLineSegment(sketch, "E17.9.0", {"start": v(1.03, -5.99) * mm, "end": v(1.03, -32.19) * mm});
            skLineSegment(sketch, "E17.9.1", {"start": v(-1.15, -5.99) * mm, "end": v(-1.15, -32.19) * mm});
            skLineSegment(sketch, "E17.10.0", {"start": v(3.87, -4.63) * mm, "end": v(16.97, -27.33) * mm});
            skLineSegment(sketch, "E17.10.1", {"start": v(1.98, -5.73) * mm, "end": v(15.08, -28.42) * mm});
            skLineSegment(sketch, "E17.11.0", {"start": v(5.65, -2.04) * mm, "end": v(28.34, -15.14) * mm});
            skLineSegment(sketch, "E17.11.1", {"start": v(4.56, -3.93) * mm, "end": v(27.25, -17.04) * mm});
            skPoint(sketch, "E17.center", {"position": v(-0.07, -0.01) * mm});
            skCircle(sketch, "E18", {"center": v(-0.07, -0.01) * mm, "radius": 6.22 * mm});
            skSolve(sketch);
        }
        {
            var Q0;
            {var subQ0=sQuery(id+"F4.wireOp",EDGE,"E17.10.0");var subQ1=sQuery(id+"F4.wireOp",EDGE,"E13");var subQ2=makeQuery(id+"F4.imprint","INTERSECT",VERTEX,{"derivedFrom":[subQ1,subQ0]});Q0=makeQuery(id+"F4.imprint","IMPRINT",FACE,{"disambiguationData":[TD([[makeQuery(id+"F4.imprint","IMPRINT",EDGE,{"disambiguationData":[TD([[subQ2,-1.0]])],"derivedFrom":subQ1}),1.0]])]});}
            var Q1;
            {var subQ0=sQuery(id+"F4.wireOp",EDGE,"E17.9.0");var subQ1=sQuery(id+"F4.wireOp",EDGE,"E13");var subQ2=makeQuery(id+"F4.imprint","INTERSECT",VERTEX,{"derivedFrom":[subQ1,subQ0]});Q1=makeQuery(id+"F4.imprint","IMPRINT",FACE,{"disambiguationData":[TD([[makeQuery(id+"F4.imprint","IMPRINT",EDGE,{"disambiguationData":[TD([[subQ2,-1.0]])],"derivedFrom":subQ1}),1.0]])]});}
            var Q2;
            {var subQ0=sQuery(id+"F4.wireOp",EDGE,"E17.8.0");var subQ1=sQuery(id+"F4.wireOp",EDGE,"E13");var subQ2=makeQuery(id+"F4.imprint","INTERSECT",VERTEX,{"derivedFrom":[subQ1,subQ0]});Q2=makeQuery(id+"F4.imprint","IMPRINT",FACE,{"disambiguationData":[TD([[makeQuery(id+"F4.imprint","IMPRINT",EDGE,{"disambiguationData":[TD([[subQ2,-1.0]])],"derivedFrom":subQ1}),1.0]])]});}
            var Q3;
            {var subQ0=sQuery(id+"F4.wireOp",EDGE,"E17.7.0");var subQ1=sQuery(id+"F4.wireOp",EDGE,"E13");var subQ2=makeQuery(id+"F4.imprint","INTERSECT",VERTEX,{"derivedFrom":[subQ1,subQ0]});Q3=makeQuery(id+"F4.imprint","IMPRINT",FACE,{"disambiguationData":[TD([[makeQuery(id+"F4.imprint","IMPRINT",EDGE,{"disambiguationData":[TD([[subQ2,-1.0]])],"derivedFrom":subQ1}),1.0]])]});}
            var Q4;
            {var subQ0=sQuery(id+"F4.wireOp",EDGE,"E17.6.0");var subQ1=sQuery(id+"F4.wireOp",EDGE,"E13");var subQ2=makeQuery(id+"F4.imprint","INTERSECT",VERTEX,{"derivedFrom":[subQ1,subQ0]});Q4=makeQuery(id+"F4.imprint","IMPRINT",FACE,{"disambiguationData":[TD([[makeQuery(id+"F4.imprint","IMPRINT",EDGE,{"disambiguationData":[TD([[subQ2,-1.0]])],"derivedFrom":subQ1}),1.0]])]});}
            var Q5;
            {var subQ0=sQuery(id+"F4.wireOp",EDGE,"E17.4.0");var subQ1=sQuery(id+"F4.wireOp",EDGE,"E13");var subQ2=makeQuery(id+"F4.imprint","INTERSECT",VERTEX,{"derivedFrom":[subQ1,subQ0]});Q5=makeQuery(id+"F4.imprint","IMPRINT",FACE,{"disambiguationData":[TD([[makeQuery(id+"F4.imprint","IMPRINT",EDGE,{"disambiguationData":[TD([[subQ2,-1.0]])],"derivedFrom":subQ1}),1.0]])]});}
            var Q6;
            {var subQ0=sQuery(id+"F4.wireOp",EDGE,"E17.3.0");var subQ1=sQuery(id+"F4.wireOp",EDGE,"E13");var subQ2=makeQuery(id+"F4.imprint","INTERSECT",VERTEX,{"derivedFrom":[subQ1,subQ0]});Q6=makeQuery(id+"F4.imprint","IMPRINT",FACE,{"disambiguationData":[TD([[makeQuery(id+"F4.imprint","IMPRINT",EDGE,{"disambiguationData":[TD([[subQ2,-1.0]])],"derivedFrom":subQ1}),1.0]])]});}
            var Q7;
            {var subQ0=sQuery(id+"F4.wireOp",EDGE,"E17.5.0");var subQ1=sQuery(id+"F4.wireOp",EDGE,"E13");var subQ2=makeQuery(id+"F4.imprint","INTERSECT",VERTEX,{"derivedFrom":[subQ1,subQ0]});Q7=makeQuery(id+"F4.imprint","IMPRINT",FACE,{"disambiguationData":[TD([[makeQuery(id+"F4.imprint","IMPRINT",EDGE,{"disambiguationData":[TD([[subQ2,-1.0]])],"derivedFrom":subQ1}),1.0]])]});}
            var Q8;
            {var subQ0=sQuery(id+"F4.wireOp",EDGE,"E17.2.0");var subQ1=sQuery(id+"F4.wireOp",EDGE,"E13");var subQ2=makeQuery(id+"F4.imprint","INTERSECT",VERTEX,{"derivedFrom":[subQ1,subQ0]});Q8=makeQuery(id+"F4.imprint","IMPRINT",FACE,{"disambiguationData":[TD([[makeQuery(id+"F4.imprint","IMPRINT",EDGE,{"disambiguationData":[TD([[subQ2,-1.0]])],"derivedFrom":subQ1}),1.0]])]});}
            var Q9;
            {var subQ0=sQuery(id+"F4.wireOp",EDGE,"E17.1.0");var subQ1=sQuery(id+"F4.wireOp",EDGE,"E13");var subQ2=makeQuery(id+"F4.imprint","INTERSECT",VERTEX,{"derivedFrom":[subQ1,subQ0]});Q9=makeQuery(id+"F4.imprint","IMPRINT",FACE,{"disambiguationData":[TD([[makeQuery(id+"F4.imprint","IMPRINT",EDGE,{"disambiguationData":[TD([[subQ2,-1.0]])],"derivedFrom":subQ1}),1.0]])]});}
            var Q10;
            {var subQ0=sQuery(id+"F4.wireOp",EDGE,"E15");var subQ1=sQuery(id+"F4.wireOp",EDGE,"E13");var subQ2=makeQuery(id+"F4.imprint","INTERSECT",VERTEX,{"derivedFrom":[subQ1,subQ0]});Q10=makeQuery(id+"F4.imprint","IMPRINT",FACE,{"disambiguationData":[TD([[makeQuery(id+"F4.imprint","IMPRINT",EDGE,{"disambiguationData":[TD([[subQ2,-1.0]])],"derivedFrom":subQ1}),1.0]])]});}
            var Q11;
            {var subQ0=sQuery(id+"F4.wireOp",EDGE,"E16.MirrorCS");var subQ1=sQuery(id+"F4.wireOp",EDGE,"E13");var subQ2=makeQuery(id+"F4.imprint","INTERSECT",VERTEX,{"derivedFrom":[subQ1,subQ0]});Q11=makeQuery(id+"F4.imprint","IMPRINT",FACE,{"disambiguationData":[TD([[makeQuery(id+"F4.imprint","IMPRINT",EDGE,{"disambiguationData":[TD([[subQ2,1.0]])],"derivedFrom":subQ1}),1.0]])]});}
            extrude(context, id + "F5", {"entities" : qUnion([Q0, Q1, Q2, Q3, Q4, Q5, Q6, Q7, Q8, Q9, Q10, Q11]), "operationType" : NewBodyOperationType.REMOVE, "oppositeDirection" : true, "depth" : 25 * mm, "offsetDistance" : 25 * mm});
        }
    });
